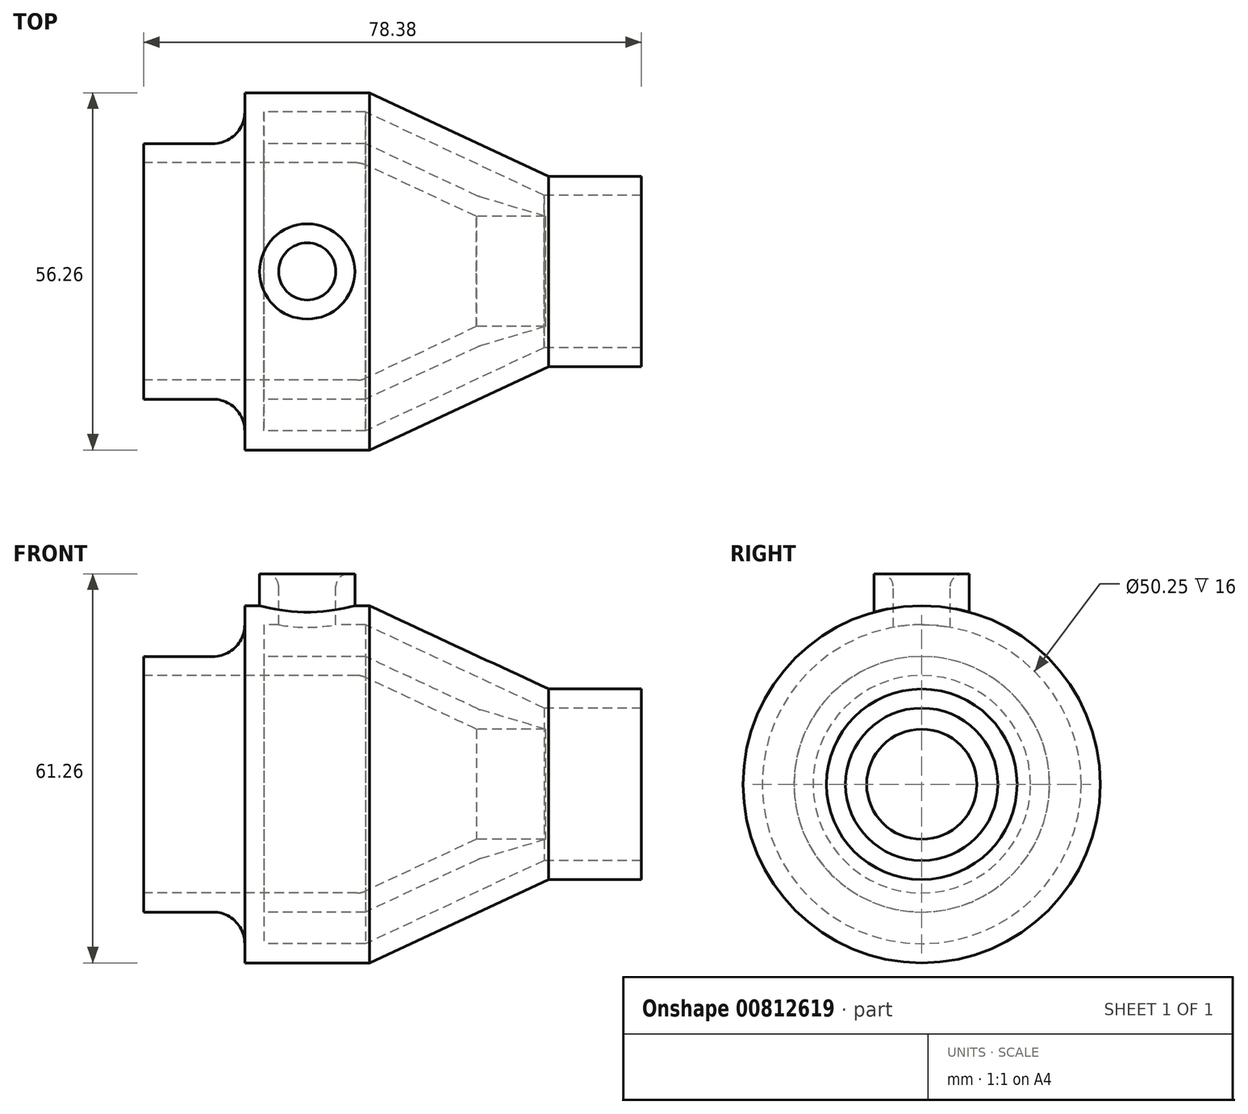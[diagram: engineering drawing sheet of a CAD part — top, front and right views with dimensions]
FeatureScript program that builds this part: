
annotation { "Feature Type Name" : "Feature", "Feature Type Description" : "" }
export const myFeature = defineFeature(function(context is Context, id is Id, definition is map)
    precondition{}
    {
        {
            var Q0;
            Q0=qCreatedBy(makeId("Front.planeOp"),FACE);
            var sketch = newSketch(context, id + "F0", { "sketchPlane" : qUnion([Q0])});
            skLineSegment(sketch, "E0", {"start": v(-63.06, 17.12) * mm, "end": v(-28.81, 17.12) * mm});
            skLineSegment(sketch, "E1", {"start": v(-28.81, 17.12) * mm, "end": v(-10.69, 8.67) * mm});
            skLineSegment(sketch, "E2.0", {"start": v(-28.15, 20.12) * mm, "end": v(-10.28, 11.8) * mm});
            skLineSegment(sketch, "E2.1", {"start": v(-63.06, 20.12) * mm, "end": v(-28.15, 20.12) * mm});
            skLineSegment(sketch, "E3", {"start": v(-10.28, 11.8) * mm, "end": v(-10.69, 8.67) * mm});
            skLineSegment(sketch, "E4", {"start": v(-63.06, 20.12) * mm, "end": v(-63.06, 17.12) * mm});
            skLineSegment(sketch, "E5", {"start": v(0, 12) * mm, "end": v(15.32, 12) * mm});
            skLineSegment(sketch, "E6", {"start": v(0, 12) * mm, "end": v(-28.15, 25.12) * mm});
            skLineSegment(sketch, "E7", {"start": v(-28.15, 25.12) * mm, "end": v(-44.15, 25.12) * mm});
            skLineSegment(sketch, "E8", {"start": v(-44.15, 25.12) * mm, "end": v(-44.15, 20.12) * mm});
            skPoint(sketch, "E8.endSnap0", {"position": v(-45.6, 20.12) * mm});
            skLineSegment(sketch, "E9.0", {"start": v(0.67, 15) * mm, "end": v(15.32, 15) * mm});
            skLineSegment(sketch, "E9.1", {"start": v(0.67, 15) * mm, "end": v(-27.48, 28.12) * mm});
            skLineSegment(sketch, "E9.2", {"start": v(-27.48, 28.12) * mm, "end": v(-47.15, 28.12) * mm});
            skLineSegment(sketch, "E9.3", {"start": v(-47.15, 28.12) * mm, "end": v(-47.15, 20.12) * mm});
            skLineSegment(sketch, "E10", {"start": v(15.32, 15) * mm, "end": v(15.32, 12) * mm});
            skLineSegment(sketch, "E11", {"start": v(-56.48, 0) * mm, "end": v(31.38, 0) * mm, "construction": true});
            skLineSegment(sketch, "E12", {"start": v(-10.69, 8.67) * mm, "end": v(0.2, 8.67) * mm});
            skLineSegment(sketch, "E13", {"start": v(-10.28, 11.8) * mm, "end": v(0.2, 8.67) * mm});
            skSolve(sketch);
        }
        {
            var Q0;
            Q0 = qSketchRegion(id + "F0", true);
            var Q1;
            Q1=sQuery(id+"F0.wireOp",EDGE,"E11");
            revolve(context, id + "F1", {"surfaceOperationType" : NewSurfaceOperationType.NEW, "entities" : qUnion([Q0]), "axis" : qUnion([Q1]), "revolveType" : RevolveType.FULL});
        }
        {
            var Q0;
            Q0=qCreatedBy(makeId("Right.planeOp"),FACE);
            var sketch = newSketch(context, id + "F2", { "sketchPlane" : qUnion([Q0])});
            skCircle(sketch, "E14.0", {"center": v(0, 0) * mm, "radius": 28.12 * mm, "construction": true});
            skLineSegment(sketch, "E15", {"start": v(32.58, 28.12) * mm, "end": v(-33.03, 28.12) * mm, "construction": true});
            skSolve(sketch);
        }
        {
            var Q0;
            Q0=makeQuery(id+"F1.opRevolve","SWEPT_FACE",FACE,{"disambiguationData":[OSD([sQuery(id+"F0.wireOp",EDGE,"E9.3")])]});
            var sketch = newSketch(context, id + "F3", { "sketchPlane" : qUnion([Q0])});
            skLineSegment(sketch, "E16.0", {"start": v(-32.58, 28.12) * mm, "end": v(33.03, 28.12) * mm, "construction": true});
            skSolve(sketch);
        }
        {
            var Q0;
            Q0=sQuery(id+"F3.wireOp",VERTEX,"E16.0.start");
            var Q1;
            Q1=sQuery(id+"F2.wireOp",VERTEX,"E15.start");
            var Q2;
            Q2=sQuery(id+"F3.wireOp",VERTEX,"E16.0.end");
            cPlane(context, id + "F4", {"entities" : qUnion([Q0, Q1, Q2]), "cplaneType" : CPlaneType.THREE_POINT, "offset" : 25 * mm, "width" : 150 * mm, "height" : 150 * mm});
        }
        {
            var Q0;
            Q0=qCreatedBy(id+"F4.planeOp",FACE);
            var sketch = newSketch(context, id + "F5", { "sketchPlane" : qUnion([Q0])});
            skLineSegment(sketch, "E17.0", {"start": v(-47.15, 32.58) * mm, "end": v(-47.15, -33.03) * mm});
            skLineSegment(sketch, "E17.1", {"start": v(-27.48, -28.12) * mm, "end": v(-27.48, 28.12) * mm});
            skLineSegment(sketch, "E18", {"start": v(-27.48, 0) * mm, "end": v(-47.15, 0) * mm, "construction": true});
            skCircle(sketch, "E19", {"center": v(-37.31, 0) * mm, "radius": 4.5 * mm});
            skCircle(sketch, "E20.0", {"center": v(-37.31, 0) * mm, "radius": 7.5 * mm});
            skSolve(sketch);
        }
        {
            var Q0;
            Q0=makeQuery(id+"F5.imprint","IMPRINT",FACE,{"disambiguationData":[TD([[makeQuery(id+"F5.imprint","IMPRINT",EDGE,{"derivedFrom":sQuery(id+"F5.wireOp",EDGE,"E19")}),1.0]])]});
            var Q1;
            Q1=makeQuery(id+"F1.opRevolve","SWEPT_FACE",FACE,{"disambiguationData":[OSD([sQuery(id+"F0.wireOp",EDGE,"E7")])]});
            extrude(context, id + "F6", {"entities" : qUnion([Q0]), "operationType" : NewBodyOperationType.REMOVE, "endBound" : BoundingType.UP_TO_SURFACE, "oppositeDirection" : true, "depth" : 25 * mm, "endBoundEntityFace" : qUnion([Q1]), "offsetDistance" : 25 * mm});
        }
        {
            var Q0;
            Q0 = qSketchRegion(id + "F5", true);
            var Q1;
            Q1=makeQuery(id+"F1.opRevolve","SWEPT_BODY",BODY,{"disambiguationData":[OSD([sQuery(id+"F0.wireOp",EDGE,"E0"),sQuery(id+"F0.wireOp",EDGE,"E1"),sQuery(id+"F0.wireOp",EDGE,"E2.0"),sQuery(id+"F0.wireOp",EDGE,"E2.1"),sQuery(id+"F0.wireOp",EDGE,"E4"),sQuery(id+"F0.wireOp",EDGE,"E5"),sQuery(id+"F0.wireOp",EDGE,"E6"),sQuery(id+"F0.wireOp",EDGE,"E7"),sQuery(id+"F0.wireOp",EDGE,"E8"),sQuery(id+"F0.wireOp",EDGE,"E9.0"),sQuery(id+"F0.wireOp",EDGE,"E9.1"),sQuery(id+"F0.wireOp",EDGE,"E9.2"),sQuery(id+"F0.wireOp",EDGE,"E9.3"),sQuery(id+"F0.wireOp",EDGE,"E10"),sQuery(id+"F0.wireOp",EDGE,"E12"),sQuery(id+"F0.wireOp",EDGE,"E13")])]});
            extrude(context, id + "F7", {"entities" : qUnion([Q0]), "operationType" : NewBodyOperationType.ADD, "depth" : 5 * mm, "offsetDistance" : 25 * mm, "hasSecondDirection" : true, "secondDirectionBound" : SecondDirectionBoundingType.UP_TO_BODY, "secondDirectionOppositeDirection" : true, "secondDirectionDepth" : 25 * mm, "secondDirectionBoundEntityBody" : qUnion([Q1])});
        }
        {
            var Q0;
            Q0=makeQuery(id+"F1.opRevolve","SWEPT_EDGE",EDGE,{"disambiguationData":[OSD([sQuery(id+"F0.wireOp",EDGE,"E2.1"),sQuery(id+"F0.wireOp",EDGE,"E9.3")])]});
            fillet(context, id + "F8", {"entities" : qUnion([Q0]), "radius" : 5 * mm, "tangentPropagation" : true, "allowEdgeOverflow" : false});
        }
        {
            var Q0;
            Q0=makeQuery(id+"F1.opRevolve","SWEPT_EDGE",EDGE,{"disambiguationData":[OSD([sQuery(id+"F0.wireOp",EDGE,"E2.0"),sQuery(id+"F0.wireOp",EDGE,"E3")])]});
            var Q1;
            Q1=makeQuery(id+"F1.opRevolve","SWEPT_EDGE",EDGE,{"disambiguationData":[OSD([sQuery(id+"F0.wireOp",EDGE,"E0"),sQuery(id+"F0.wireOp",EDGE,"E1")])]});
            fillet(context, id + "F9", {"entities" : qUnion([Q0, Q1]), "radius" : 3 * mm, "tangentPropagation" : true, "allowEdgeOverflow" : false});
        }
        {
            var Q0;
            Q0=makeQuery(id+"F7.opExtrude","CAP_EDGE",EDGE,{"disambiguationData":[OSD([sQuery(id+"F5.wireOp",EDGE,"E20.0")]),topologyDisambiguationEdgeConnected([makeQuery(id+"F1.opRevolve","SWEPT_FACE",FACE,{"disambiguationData":[OSD([sQuery(id+"F0.wireOp",EDGE,"E9.2")])]})])],"isStart":false});
            var Q1;
            Q1=makeQuery(id+"F7.opExtrude","CAP_EDGE",EDGE,{"disambiguationData":[OSD([sQuery(id+"F5.wireOp",EDGE,"E19")])],"isStart":false});
            fillet(context, id + "F10", {"entities" : qUnion([Q0, Q1]), "radius" : 2 * mm, "tangentPropagation" : true, "allowEdgeOverflow" : false});
        }
    });
